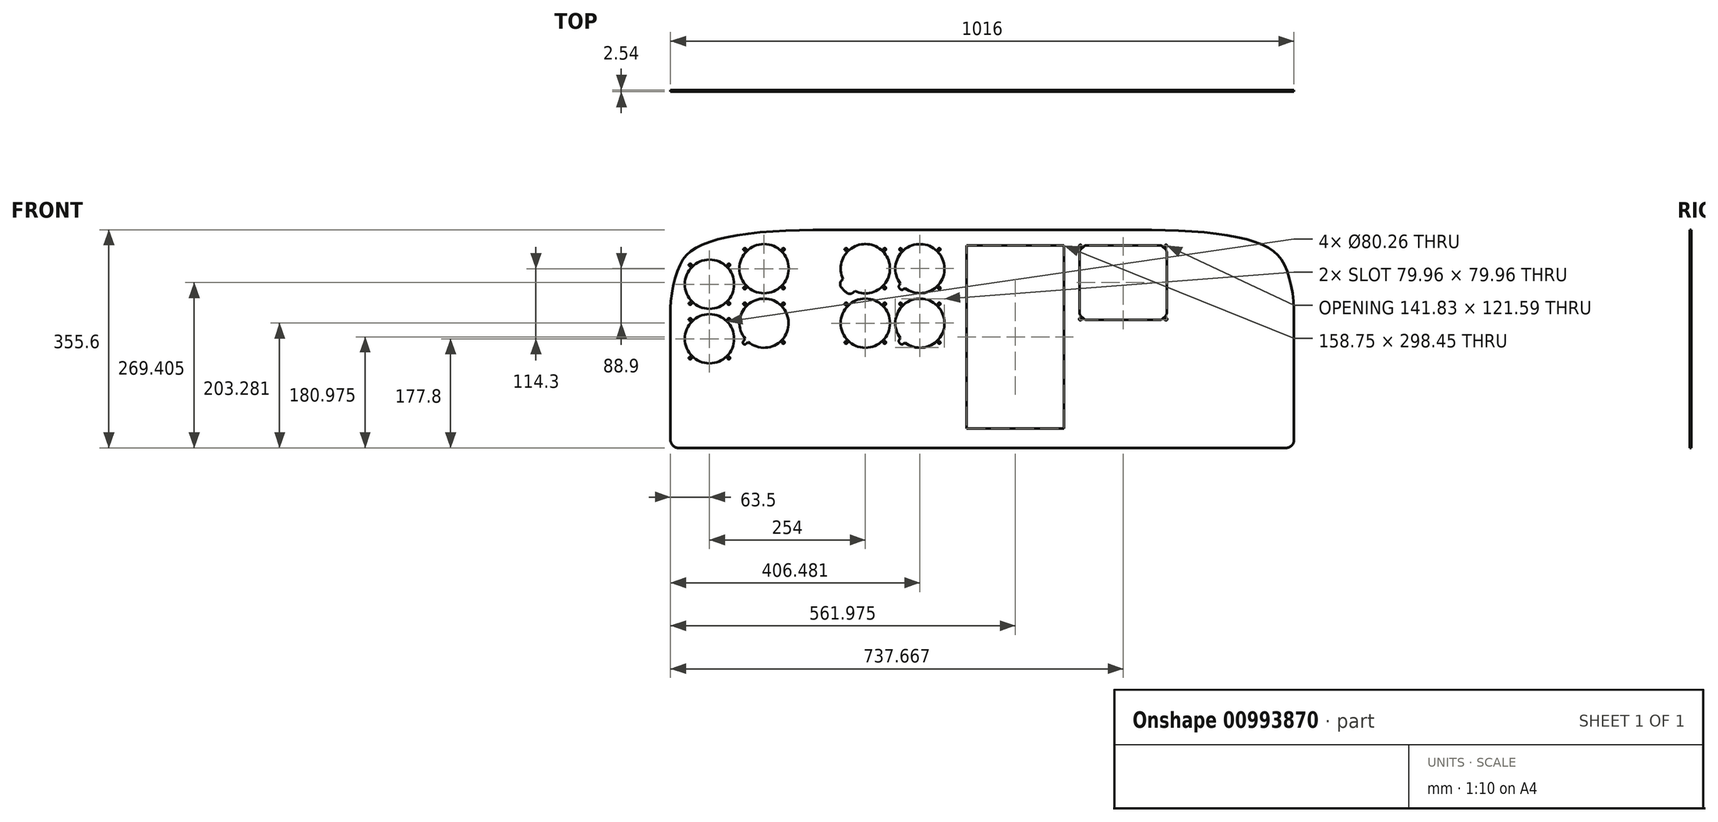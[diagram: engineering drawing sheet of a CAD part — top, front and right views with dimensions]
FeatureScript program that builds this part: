
annotation { "Feature Type Name" : "Feature", "Feature Type Description" : "" }
export const myFeature = defineFeature(function(context is Context, id is Id, definition is map)
    precondition{}
    {
        {
            var Q0;
            Q0=qCreatedBy(makeId("Front.planeOp"),FACE);
            var sketch = newSketch(context, id + "F0", { "sketchPlane" : qUnion([Q0])});
            skLineSegment(sketch, "E0.bottom", {"start": v(12.7, 0) * mm, "end": v(1003.3, 0) * mm});
            skLineSegment(sketch, "E0.top", {"start": v(276.91, 355.6) * mm, "end": v(739.09, 355.6) * mm});
            skLineSegment(sketch, "E0.left", {"start": v(0, 12.7) * mm, "end": v(0, 228.6) * mm});
            skLineSegment(sketch, "E0.right", {"start": v(1016, 0) * mm, "end": v(1016, 228.6) * mm});
            skPoint(sketch, "E1", {"position": v(12.7, 292.1) * mm});
            skPoint(sketch, "E2", {"position": v(38.1, 323.85) * mm});
            skPoint(sketch, "E3", {"position": v(127, 349.25) * mm});
            skFitSpline(sketch, "E4", {"points": [v(0, 228.6) * mm, v(12.7, 292.1) * mm, v(38.1, 323.85) * mm, v(127, 349.25) * mm, v(330.2, 355.6) * mm], "startDerivative": vector(0, 255.25) * mm, "endDerivative": vector(510.23, 0.47) * mm});
            skLineSegment(sketch, "E5", {"start": v(508, 450.84) * mm, "end": v(508, -240.63) * mm, "construction": true});
            skPoint(sketch, "E6.MirrorP", {"position": v(889, 349.25) * mm});
            skLineSegment(sketch, "E7.MirrorCS", {"start": v(739.09, 355.6) * mm, "end": v(276.91, 355.6) * mm});
            skLineSegment(sketch, "E8.MirrorCS", {"start": v(1016, 12.7) * mm, "end": v(1016, 228.6) * mm});
            skPoint(sketch, "E9.MirrorP", {"position": v(977.9, 323.85) * mm});
            skFitSpline(sketch, "E10.MirrorCS", {"points": [v(1016, 228.6) * mm, v(1003.3, 292.1) * mm, v(977.9, 323.85) * mm, v(889, 349.25) * mm, v(685.8, 355.6) * mm], "startDerivative": vector(0, 255.25) * mm, "endDerivative": vector(-510.23, 0.47) * mm});
            skPoint(sketch, "E11.orphan", {"position": v(1016, 355.6) * mm});
            skPoint(sketch, "E12.orphan", {"position": v(0, 355.6) * mm});
            skPoint(sketch, "E13.visualSharp", {"position": v(0, 0) * mm});
            skArc(sketch, "E13.filletArc", {"start": v(0, 12.7) * mm, "mid": v(3.72, 3.72) * mm, "end": v(12.7, 0) * mm});
            skPoint(sketch, "E14.visualSharp", {"position": v(1016, 0) * mm});
            skArc(sketch, "E14.filletArc", {"start": v(1003.3, 0) * mm, "mid": v(1012.28, 3.72) * mm, "end": v(1016, 12.7) * mm});
            skSolve(sketch);
        }
        {
            var Q0;
            Q0=makeQuery(id+"F0.imprint","IMPRINT",FACE,{"disambiguationData":[TD([[makeQuery(id+"F0.imprint","IMPRINT",EDGE,{"derivedFrom":sQuery(id+"F0.wireOp",EDGE,"E0.bottom")}),1.0]])]});
            extrude(context, id + "F1", {"entities" : qUnion([Q0]), "depth" : 2.54 * mm, "offsetDistance" : 25.4 * mm});
        }
        {
            var Q0;
            Q0=makeQuery(id+"F1.opExtrude","CAP_FACE",FACE,{"disambiguationData":[OSD([sQuery(id+"F0.wireOp",EDGE,"E0.bottom"),sQuery(id+"F0.wireOp",EDGE,"E0.left"),sQuery(id+"F0.wireOp",EDGE,"E4"),sQuery(id+"F0.wireOp",EDGE,"E7.MirrorCS"),sQuery(id+"F0.wireOp",EDGE,"E8.MirrorCS"),sQuery(id+"F0.wireOp",EDGE,"E10.MirrorCS"),sQuery(id+"F0.wireOp",EDGE,"E13.filletArc"),sQuery(id+"F0.wireOp",EDGE,"E14.filletArc")])],"isStart":false});
            var sketch = newSketch(context, id + "F2", { "sketchPlane" : qUnion([Q0])});
            skPoint(sketch, "E15", {"position": v(406.4, 292.1) * mm});
            skArc(sketch, "E16", {"start": v(381.89, 260.39) * mm, "mid": v(434.74, 320.44) * mm, "end": v(374.69, 267.59) * mm});
            skLineSegment(sketch, "E17", {"start": v(285.66, 171.36) * mm, "end": v(527.14, 412.84) * mm, "construction": true});
            skLineSegment(sketch, "E18", {"start": v(373.54, 266.44) * mm, "end": v(374.69, 267.59) * mm});
            skLineSegment(sketch, "E19", {"start": v(380.74, 259.24) * mm, "end": v(381.89, 260.39) * mm});
            skArc(sketch, "E20", {"start": v(373.54, 266.44) * mm, "mid": v(373.54, 259.24) * mm, "end": v(380.74, 259.24) * mm});
            skLineSegment(sketch, "E21", {"start": v(406.4, 414.98) * mm, "end": v(406.4, 169.22) * mm, "construction": true});
            skCircle(sketch, "E22", {"center": v(437.9, 323.6) * mm, "radius": 1.98 * mm});
            skCircle(sketch, "E23.1.0", {"center": v(374.9, 323.6) * mm, "radius": 1.98 * mm});
            skLineSegment(sketch, "E23.anchor1", {"start": v(406.4, 292.1) * mm, "end": v(437.9, 323.6) * mm, "construction": true});
            skLineSegment(sketch, "E23.anchor2", {"start": v(406.4, 292.1) * mm, "end": v(374.9, 323.6) * mm, "construction": true});
            skCircle(sketch, "E24.MirrorC", {"center": v(437.9, 260.6) * mm, "radius": 1.98 * mm});
            skPoint(sketch, "E25", {"position": v(406.4, 203.2) * mm});
            skArc(sketch, "E26", {"start": v(381.89, 171.49) * mm, "mid": v(434.74, 231.54) * mm, "end": v(374.69, 178.69) * mm});
            skLineSegment(sketch, "E27", {"start": v(285.66, 82.46) * mm, "end": v(527.14, 323.94) * mm, "construction": true});
            skLineSegment(sketch, "E28", {"start": v(373.54, 177.54) * mm, "end": v(374.69, 178.69) * mm});
            skLineSegment(sketch, "E29", {"start": v(380.74, 170.34) * mm, "end": v(381.89, 171.49) * mm});
            skArc(sketch, "E30", {"start": v(373.54, 177.54) * mm, "mid": v(373.54, 170.34) * mm, "end": v(380.74, 170.34) * mm});
            skLineSegment(sketch, "E31", {"start": v(406.4, 326.08) * mm, "end": v(406.4, 80.32) * mm, "construction": true});
            skCircle(sketch, "E32", {"center": v(437.9, 234.7) * mm, "radius": 1.98 * mm});
            skCircle(sketch, "E33.1.0", {"center": v(374.9, 234.7) * mm, "radius": 1.98 * mm});
            skLineSegment(sketch, "E33.anchor1", {"start": v(406.4, 203.2) * mm, "end": v(437.9, 234.7) * mm, "construction": true});
            skLineSegment(sketch, "E33.anchor2", {"start": v(406.4, 203.2) * mm, "end": v(374.9, 234.7) * mm, "construction": true});
            skCircle(sketch, "E34.MirrorC", {"center": v(437.9, 171.7) * mm, "radius": 1.98 * mm});
            skSolve(sketch);
        }
        {
            var Q0;
            Q0 = qSketchRegion(id + "F2", true);
            extrude(context, id + "F3", {"entities" : qUnion([Q0]), "operationType" : NewBodyOperationType.REMOVE, "endBound" : BoundingType.THROUGH_ALL, "oppositeDirection" : true, "depth" : 25.4 * mm, "offsetDistance" : 25.4 * mm});
        }
        {
            var Q0;
            Q0=makeQuery(id+"F1.opExtrude","CAP_FACE",FACE,{"disambiguationData":[OSD([sQuery(id+"F0.wireOp",EDGE,"E0.bottom"),sQuery(id+"F0.wireOp",EDGE,"E0.left"),sQuery(id+"F0.wireOp",EDGE,"E4"),sQuery(id+"F0.wireOp",EDGE,"E7.MirrorCS"),sQuery(id+"F0.wireOp",EDGE,"E8.MirrorCS"),sQuery(id+"F0.wireOp",EDGE,"E10.MirrorCS"),sQuery(id+"F0.wireOp",EDGE,"E13.filletArc"),sQuery(id+"F0.wireOp",EDGE,"E14.filletArc")])],"isStart":false});
            var sketch = newSketch(context, id + "F4", { "sketchPlane" : qUnion([Q0])});
            skArc(sketch, "E35", {"start": v(300.53, 255.73) * mm, "mid": v(345.88, 320.48) * mm, "end": v(281.13, 275.13) * mm});
            skCircle(sketch, "E36", {"center": v(286.07, 323.53) * mm, "radius": 2.15 * mm});
            skCircle(sketch, "E37.1.0", {"center": v(348.93, 323.53) * mm, "radius": 2.15 * mm});
            skCircle(sketch, "E37.2.0", {"center": v(348.93, 260.67) * mm, "radius": 2.15 * mm});
            skLineSegment(sketch, "E37.anchor1", {"start": v(317.5, 292.1) * mm, "end": v(287.6, 322) * mm, "construction": true});
            skLineSegment(sketch, "E37.anchor2", {"start": v(317.5, 292.1) * mm, "end": v(348.93, 260.67) * mm, "construction": true});
            skPoint(sketch, "E38", {"position": v(292.39, 259.3) * mm});
            skPoint(sketch, "E39", {"position": v(286.53, 253.44) * mm});
            skArc(sketch, "E40", {"start": v(288.26, 252.12) * mm, "mid": v(293.48, 251.1) * mm, "end": v(298.24, 253.44) * mm});
            skLineSegment(sketch, "E41.trimOffspring", {"start": v(297.3, 252.5) * mm, "end": v(300.53, 255.73) * mm});
            skPoint(sketch, "E42.MirrorP", {"position": v(260.07, 270.74) * mm});
            skPoint(sketch, "E43.MirrorP", {"position": v(284.7, 266.99) * mm});
            skArc(sketch, "E44.MirrorCS", {"start": v(277.52, 262.86) * mm, "mid": v(276.5, 268.08) * mm, "end": v(278.84, 272.84) * mm});
            skLineSegment(sketch, "E45.MirrorCS", {"start": v(278.84, 272.84) * mm, "end": v(281.13, 275.13) * mm});
            skArc(sketch, "E46.MirrorCS", {"start": v(281.13, 275.13) * mm, "mid": v(345.88, 320.48) * mm, "end": v(300.53, 255.73) * mm});
            skArc(sketch, "E47.trimOffspring", {"start": v(277.52, 262.86) * mm, "mid": v(282.48, 257.08) * mm, "end": v(288.26, 252.12) * mm});
            skPoint(sketch, "E48.orphan", {"position": v(277.9, 271.9) * mm});
            skArc(sketch, "E49.trimOffspring", {"start": v(288.26, 252.12) * mm, "mid": v(282.48, 257.08) * mm, "end": v(277.52, 262.86) * mm});
            skPoint(sketch, "E50.orphan", {"position": v(333.75, 266.68) * mm});
            skPoint(sketch, "E51.MirrorCS.start.orphan", {"position": v(263.7, 336.73) * mm});
            skArc(sketch, "E52.trimOffspring", {"start": v(277.9, 271.9) * mm, "mid": v(286.07, 260.67) * mm, "end": v(297.3, 252.5) * mm, "construction": true});
            skLineSegment(sketch, "E53.trimOffspring", {"start": v(287.6, 322) * mm, "end": v(345.88, 263.72) * mm, "construction": true});
            skLineSegment(sketch, "E54.trimOffspring", {"start": v(284.55, 325.05) * mm, "end": v(286.07, 323.53) * mm, "construction": true});
            skArc(sketch, "E55.trimOffspring", {"start": v(297.3, 252.5) * mm, "mid": v(286.07, 260.67) * mm, "end": v(277.9, 271.9) * mm, "construction": true});
            skSolve(sketch);
        }
        {
            var Q0;
            Q0 = qSketchRegion(id + "F4", true);
            extrude(context, id + "F5", {"entities" : qUnion([Q0]), "operationType" : NewBodyOperationType.REMOVE, "endBound" : BoundingType.THROUGH_ALL, "oppositeDirection" : true, "depth" : 25.4 * mm, "offsetDistance" : 25.4 * mm});
        }
        {
            var Q0;
            Q0=makeQuery(id+"F1.opExtrude","CAP_FACE",FACE,{"disambiguationData":[OSD([sQuery(id+"F0.wireOp",EDGE,"E0.bottom"),sQuery(id+"F0.wireOp",EDGE,"E0.left"),sQuery(id+"F0.wireOp",EDGE,"E4"),sQuery(id+"F0.wireOp",EDGE,"E7.MirrorCS"),sQuery(id+"F0.wireOp",EDGE,"E8.MirrorCS"),sQuery(id+"F0.wireOp",EDGE,"E10.MirrorCS"),sQuery(id+"F0.wireOp",EDGE,"E13.filletArc"),sQuery(id+"F0.wireOp",EDGE,"E14.filletArc")])],"isStart":false});
            var sketch = newSketch(context, id + "F6", { "sketchPlane" : qUnion([Q0])});
            skLineSegment(sketch, "E56.bottom", {"start": v(482.6, 330.2) * mm, "end": v(641.35, 330.2) * mm});
            skLineSegment(sketch, "E56.top", {"start": v(482.6, 31.75) * mm, "end": v(641.35, 31.75) * mm});
            skLineSegment(sketch, "E56.left", {"start": v(482.6, 330.2) * mm, "end": v(482.6, 31.75) * mm});
            skLineSegment(sketch, "E56.right", {"start": v(641.35, 330.2) * mm, "end": v(641.35, 31.75) * mm});
            skSolve(sketch);
        }
        {
            var Q0;
            Q0 = qSketchRegion(id + "F6", true);
            extrude(context, id + "F7", {"entities" : qUnion([Q0]), "operationType" : NewBodyOperationType.REMOVE, "endBound" : BoundingType.THROUGH_ALL, "oppositeDirection" : true, "depth" : 25.4 * mm, "offsetDistance" : 25.4 * mm});
        }
        {
            var Q0;
            Q0=makeQuery(id+"F1.opExtrude","CAP_FACE",FACE,{"disambiguationData":[OSD([sQuery(id+"F0.wireOp",EDGE,"E0.bottom"),sQuery(id+"F0.wireOp",EDGE,"E0.left"),sQuery(id+"F0.wireOp",EDGE,"E4"),sQuery(id+"F0.wireOp",EDGE,"E7.MirrorCS"),sQuery(id+"F0.wireOp",EDGE,"E8.MirrorCS"),sQuery(id+"F0.wireOp",EDGE,"E10.MirrorCS"),sQuery(id+"F0.wireOp",EDGE,"E13.filletArc"),sQuery(id+"F0.wireOp",EDGE,"E14.filletArc")])],"isStart":false});
            var sketch = newSketch(context, id + "F8", { "sketchPlane" : qUnion([Q0])});
            skCircle(sketch, "E57", {"center": v(152.4, 292.1) * mm, "radius": 40.13 * mm});
            skCircle(sketch, "E58", {"center": v(152.4, 292.1) * mm, "radius": 44.45 * mm, "construction": true});
            skLineSegment(sketch, "E59", {"start": v(72.14, 372.36) * mm, "end": v(229.69, 214.81) * mm, "construction": true});
            skCircle(sketch, "E60", {"center": v(120.97, 323.53) * mm, "radius": 2.15 * mm});
            skCircle(sketch, "E61.1.0", {"center": v(183.83, 323.53) * mm, "radius": 2.15 * mm});
            skCircle(sketch, "E61.2.0", {"center": v(183.83, 260.67) * mm, "radius": 2.15 * mm});
            skCircle(sketch, "E61.3.0", {"center": v(120.97, 260.67) * mm, "radius": 2.15 * mm});
            skLineSegment(sketch, "E61.anchor1", {"start": v(152.4, 292.1) * mm, "end": v(120.97, 323.53) * mm, "construction": true});
            skLineSegment(sketch, "E61.anchor2", {"start": v(152.4, 292.1) * mm, "end": v(120.97, 260.67) * mm, "construction": true});
            skCircle(sketch, "E62", {"center": v(63.5, 266.7) * mm, "radius": 40.13 * mm});
            skCircle(sketch, "E63", {"center": v(63.5, 266.7) * mm, "radius": 44.45 * mm, "construction": true});
            skLineSegment(sketch, "E64", {"start": v(-16.76, 346.96) * mm, "end": v(140.79, 189.41) * mm, "construction": true});
            skCircle(sketch, "E65", {"center": v(32.07, 298.13) * mm, "radius": 2.15 * mm});
            skCircle(sketch, "E66.1.0", {"center": v(94.93, 298.13) * mm, "radius": 2.15 * mm});
            skCircle(sketch, "E66.2.0", {"center": v(94.93, 235.27) * mm, "radius": 2.15 * mm});
            skCircle(sketch, "E66.3.0", {"center": v(32.07, 235.27) * mm, "radius": 2.15 * mm});
            skLineSegment(sketch, "E66.anchor1", {"start": v(63.5, 266.7) * mm, "end": v(32.07, 298.13) * mm, "construction": true});
            skLineSegment(sketch, "E66.anchor2", {"start": v(63.5, 266.7) * mm, "end": v(32.07, 235.27) * mm, "construction": true});
            skCircle(sketch, "E67", {"center": v(63.5, 177.8) * mm, "radius": 40.13 * mm});
            skCircle(sketch, "E68", {"center": v(63.5, 177.8) * mm, "radius": 44.45 * mm, "construction": true});
            skLineSegment(sketch, "E69", {"start": v(-16.76, 258.06) * mm, "end": v(140.79, 100.51) * mm, "construction": true});
            skCircle(sketch, "E70", {"center": v(32.07, 209.23) * mm, "radius": 2.15 * mm});
            skCircle(sketch, "E71.1.0", {"center": v(94.93, 209.23) * mm, "radius": 2.15 * mm});
            skCircle(sketch, "E71.2.0", {"center": v(94.93, 146.37) * mm, "radius": 2.15 * mm});
            skCircle(sketch, "E71.3.0", {"center": v(32.07, 146.37) * mm, "radius": 2.15 * mm});
            skLineSegment(sketch, "E71.anchor1", {"start": v(63.5, 177.8) * mm, "end": v(32.07, 209.23) * mm, "construction": true});
            skLineSegment(sketch, "E71.anchor2", {"start": v(63.5, 177.8) * mm, "end": v(32.07, 146.37) * mm, "construction": true});
            skCircle(sketch, "E72", {"center": v(317.5, 203.2) * mm, "radius": 40.13 * mm});
            skCircle(sketch, "E73", {"center": v(317.5, 203.2) * mm, "radius": 44.45 * mm, "construction": true});
            skLineSegment(sketch, "E74", {"start": v(237.24, 283.46) * mm, "end": v(394.79, 125.91) * mm, "construction": true});
            skCircle(sketch, "E75", {"center": v(286.07, 234.63) * mm, "radius": 2.15 * mm});
            skCircle(sketch, "E76.1.0", {"center": v(348.93, 234.63) * mm, "radius": 2.15 * mm});
            skCircle(sketch, "E76.2.0", {"center": v(348.93, 171.77) * mm, "radius": 2.15 * mm});
            skCircle(sketch, "E76.3.0", {"center": v(286.07, 171.77) * mm, "radius": 2.15 * mm});
            skLineSegment(sketch, "E76.anchor1", {"start": v(317.5, 203.2) * mm, "end": v(286.07, 234.63) * mm, "construction": true});
            skLineSegment(sketch, "E76.anchor2", {"start": v(317.5, 203.2) * mm, "end": v(286.07, 171.77) * mm, "construction": true});
            skSolve(sketch);
        }
        {
            var Q0;
            Q0 = qSketchRegion(id + "F8", true);
            extrude(context, id + "F9", {"entities" : qUnion([Q0]), "operationType" : NewBodyOperationType.REMOVE, "endBound" : BoundingType.THROUGH_ALL, "oppositeDirection" : true, "depth" : 25.4 * mm, "offsetDistance" : 25.4 * mm});
        }
        {
            var Q0;
            Q0=makeQuery(id+"F1.opExtrude","CAP_FACE",FACE,{"disambiguationData":[OSD([sQuery(id+"F0.wireOp",EDGE,"E0.bottom"),sQuery(id+"F0.wireOp",EDGE,"E0.left"),sQuery(id+"F0.wireOp",EDGE,"E4"),sQuery(id+"F0.wireOp",EDGE,"E7.MirrorCS"),sQuery(id+"F0.wireOp",EDGE,"E8.MirrorCS"),sQuery(id+"F0.wireOp",EDGE,"E10.MirrorCS"),sQuery(id+"F0.wireOp",EDGE,"E13.filletArc"),sQuery(id+"F0.wireOp",EDGE,"E14.filletArc")])],"isStart":false});
            var sketch = newSketch(context, id + "F10", { "sketchPlane" : qUnion([Q0])});
            skLineSegment(sketch, "E77", {"start": v(92.33, 263.27) * mm, "end": v(212.47, 143.13) * mm, "construction": true});
            skArc(sketch, "E78", {"start": v(126.45, 172.76) * mm, "mid": v(180.69, 231.49) * mm, "end": v(121.96, 177.25) * mm});
            skCircle(sketch, "E79", {"center": v(152.4, 203.2) * mm, "radius": 44.45 * mm, "construction": true});
            skCircle(sketch, "E80", {"center": v(120.97, 234.63) * mm, "radius": 2.15 * mm});
            skCircle(sketch, "E81.1.0", {"center": v(183.83, 234.63) * mm, "radius": 2.15 * mm});
            skCircle(sketch, "E81.2.0", {"center": v(183.83, 171.77) * mm, "radius": 2.15 * mm});
            skLineSegment(sketch, "E81.anchor1", {"start": v(152.4, 203.2) * mm, "end": v(120.97, 234.63) * mm, "construction": true});
            skLineSegment(sketch, "E81.anchor2", {"start": v(152.4, 203.2) * mm, "end": v(183.83, 171.77) * mm, "construction": true});
            skLineSegment(sketch, "E82", {"start": v(103.05, 153.85) * mm, "end": v(152.4, 203.2) * mm, "construction": true});
            skArc(sketch, "E83", {"start": v(118.8, 174.1) * mm, "mid": v(118.72, 169.52) * mm, "end": v(123.3, 169.6) * mm});
            skLineSegment(sketch, "E84", {"start": v(118.72, 174.01) * mm, "end": v(121.96, 177.25) * mm});
            skLineSegment(sketch, "E85", {"start": v(123.21, 169.52) * mm, "end": v(126.45, 172.76) * mm});
            skSolve(sketch);
        }
        {
            var Q0;
            Q0 = qSketchRegion(id + "F10", true);
            extrude(context, id + "F11", {"entities" : qUnion([Q0]), "operationType" : NewBodyOperationType.REMOVE, "endBound" : BoundingType.THROUGH_ALL, "oppositeDirection" : true, "depth" : 25.4 * mm, "offsetDistance" : 25.4 * mm});
        }
        {
            var Q0;
            Q0=makeQuery(id+"F1.opExtrude","CAP_FACE",FACE,{"disambiguationData":[OSD([sQuery(id+"F0.wireOp",EDGE,"E0.bottom"),sQuery(id+"F0.wireOp",EDGE,"E0.left"),sQuery(id+"F0.wireOp",EDGE,"E4"),sQuery(id+"F0.wireOp",EDGE,"E7.MirrorCS"),sQuery(id+"F0.wireOp",EDGE,"E8.MirrorCS"),sQuery(id+"F0.wireOp",EDGE,"E10.MirrorCS"),sQuery(id+"F0.wireOp",EDGE,"E13.filletArc"),sQuery(id+"F0.wireOp",EDGE,"E14.filletArc")])],"isStart":false});
            var sketch = newSketch(context, id + "F12", { "sketchPlane" : qUnion([Q0])});
            skLineSegment(sketch, "E86.bottom", {"start": v(677.86, 208.61) * mm, "end": v(797.47, 208.61) * mm});
            skLineSegment(sketch, "E86.top", {"start": v(677.86, 330.2) * mm, "end": v(797.47, 330.2) * mm});
            skLineSegment(sketch, "E86.left", {"start": v(666.75, 219.73) * mm, "end": v(666.75, 319.09) * mm});
            skLineSegment(sketch, "E86.right", {"start": v(808.58, 219.73) * mm, "end": v(808.58, 319.09) * mm});
            skLineSegment(sketch, "E87", {"start": v(801.96, 328.34) * mm, "end": v(806.72, 323.58) * mm});
            skLineSegment(sketch, "E88", {"start": v(806.72, 215.23) * mm, "end": v(801.96, 210.47) * mm});
            skLineSegment(sketch, "E89", {"start": v(673.37, 210.47) * mm, "end": v(668.6, 215.23) * mm});
            skLineSegment(sketch, "E90", {"start": v(668.6, 323.58) * mm, "end": v(673.37, 328.34) * mm});
            skPoint(sketch, "E91", {"position": v(737.67, 269.4) * mm});
            skLineSegment(sketch, "E92", {"start": v(671, 212.85) * mm, "end": v(660.56, 202.42) * mm, "construction": true});
            skCircle(sketch, "E93", {"center": v(667.9, 209.76) * mm, "radius": 2.03 * mm});
            skCircle(sketch, "E94.MirrorC", {"center": v(807.43, 209.76) * mm, "radius": 2.03 * mm});
            skCircle(sketch, "E95.MirrorC", {"center": v(807.44, 329.05) * mm, "radius": 2.03 * mm});
            skCircle(sketch, "E96.MirrorC", {"center": v(667.9, 329.05) * mm, "radius": 2.03 * mm});
            skPoint(sketch, "E97.visualSharp", {"position": v(800.1, 330.2) * mm});
            skArc(sketch, "E97.filletArc", {"start": v(801.96, 328.34) * mm, "mid": v(799.9, 329.72) * mm, "end": v(797.47, 330.2) * mm});
            skPoint(sketch, "E98.visualSharp", {"position": v(808.58, 321.72) * mm});
            skArc(sketch, "E98.filletArc", {"start": v(808.58, 319.09) * mm, "mid": v(808.1, 321.52) * mm, "end": v(806.72, 323.58) * mm});
            skPoint(sketch, "E99.visualSharp", {"position": v(808.58, 217.1) * mm});
            skArc(sketch, "E99.filletArc", {"start": v(806.72, 215.23) * mm, "mid": v(808.1, 217.3) * mm, "end": v(808.58, 219.73) * mm});
            skPoint(sketch, "E100.visualSharp", {"position": v(800.1, 208.61) * mm});
            skArc(sketch, "E100.filletArc", {"start": v(797.47, 208.61) * mm, "mid": v(799.9, 209.1) * mm, "end": v(801.96, 210.47) * mm});
            skPoint(sketch, "E101.visualSharp", {"position": v(675.23, 208.61) * mm});
            skArc(sketch, "E101.filletArc", {"start": v(673.37, 210.47) * mm, "mid": v(675.43, 209.1) * mm, "end": v(677.86, 208.61) * mm});
            skPoint(sketch, "E102.visualSharp", {"position": v(666.75, 217.1) * mm});
            skArc(sketch, "E102.filletArc", {"start": v(666.75, 219.73) * mm, "mid": v(667.23, 217.3) * mm, "end": v(668.6, 215.23) * mm});
            skPoint(sketch, "E103.visualSharp", {"position": v(666.75, 321.72) * mm});
            skArc(sketch, "E103.filletArc", {"start": v(668.6, 323.58) * mm, "mid": v(667.23, 321.52) * mm, "end": v(666.75, 319.09) * mm});
            skPoint(sketch, "E104.visualSharp", {"position": v(675.23, 330.2) * mm});
            skArc(sketch, "E104.filletArc", {"start": v(677.86, 330.2) * mm, "mid": v(675.43, 329.72) * mm, "end": v(673.37, 328.34) * mm});
            skLineSegment(sketch, "E105", {"start": v(667.9, 329.05) * mm, "end": v(671, 325.96) * mm, "construction": true});
            skLineSegment(sketch, "E106", {"start": v(807.43, 209.76) * mm, "end": v(804.34, 212.85) * mm, "construction": true});
            skLineSegment(sketch, "E107", {"start": v(807.44, 329.05) * mm, "end": v(804.34, 325.96) * mm, "construction": true});
            skSolve(sketch);
        }
        {
            var Q0;
            Q0 = qSketchRegion(id + "F12", true);
            extrude(context, id + "F13", {"entities" : qUnion([Q0]), "operationType" : NewBodyOperationType.REMOVE, "endBound" : BoundingType.THROUGH_ALL, "oppositeDirection" : true, "depth" : 25.4 * mm, "offsetDistance" : 25.4 * mm});
        }
    });
